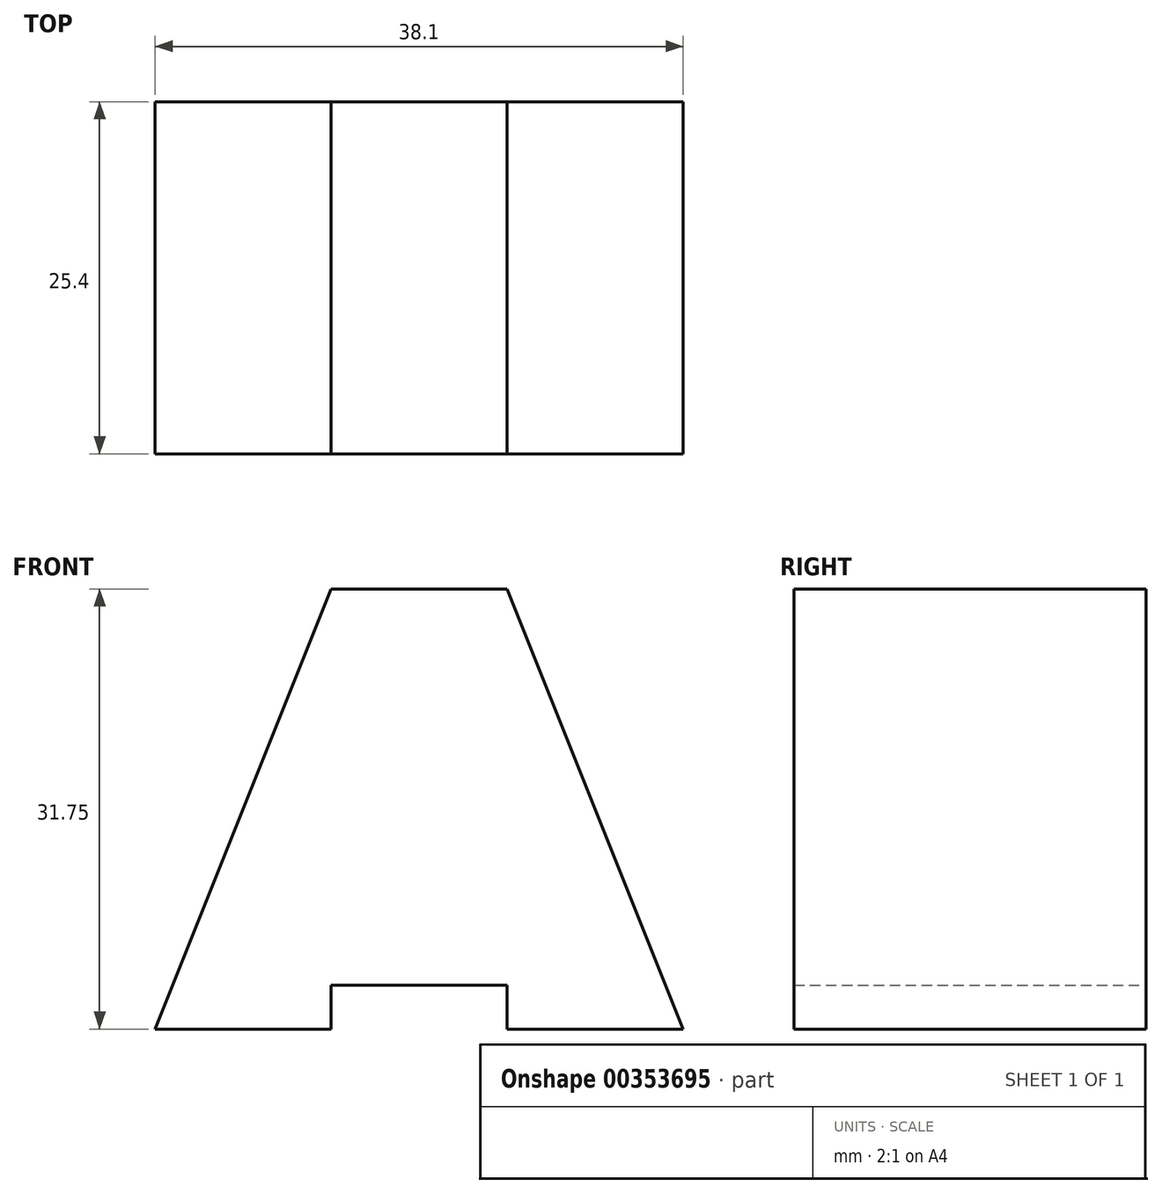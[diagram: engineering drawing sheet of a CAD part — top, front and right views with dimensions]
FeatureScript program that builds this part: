
annotation { "Feature Type Name" : "Feature", "Feature Type Description" : "" }
export const myFeature = defineFeature(function(context is Context, id is Id, definition is map)
    precondition{}
    {
        {
            var Q0;
            Q0=qCreatedBy(makeId("Front.planeOp"),FACE);
            var sketch = newSketch(context, id + "F0", { "sketchPlane" : qUnion([Q0])});
            skLineSegment(sketch, "E0", {"start": v(-44.03, 21.31) * mm, "end": v(-31.33, 21.31) * mm});
            skLineSegment(sketch, "E1", {"start": v(-31.33, 21.31) * mm, "end": v(-31.33, 24.49) * mm});
            skLineSegment(sketch, "E2", {"start": v(-31.33, 24.49) * mm, "end": v(-18.63, 24.49) * mm});
            skLineSegment(sketch, "E3", {"start": v(-18.63, 24.49) * mm, "end": v(-18.63, 21.31) * mm});
            skLineSegment(sketch, "E4", {"start": v(-18.63, 21.31) * mm, "end": v(-5.93, 21.31) * mm});
            skLineSegment(sketch, "E5", {"start": v(-5.93, 21.31) * mm, "end": v(-18.63, 53.06) * mm});
            skLineSegment(sketch, "E6", {"start": v(-18.63, 53.06) * mm, "end": v(-31.33, 53.06) * mm});
            skLineSegment(sketch, "E7", {"start": v(-31.33, 53.06) * mm, "end": v(-44.03, 21.31) * mm});
            skSolve(sketch);
        }
        {
            var Q0;
            Q0 = qSketchRegion(id + "F0", true);
            extrude(context, id + "F1", {"entities" : qUnion([Q0]), "depth" : 25.4 * mm});
        }
    });
